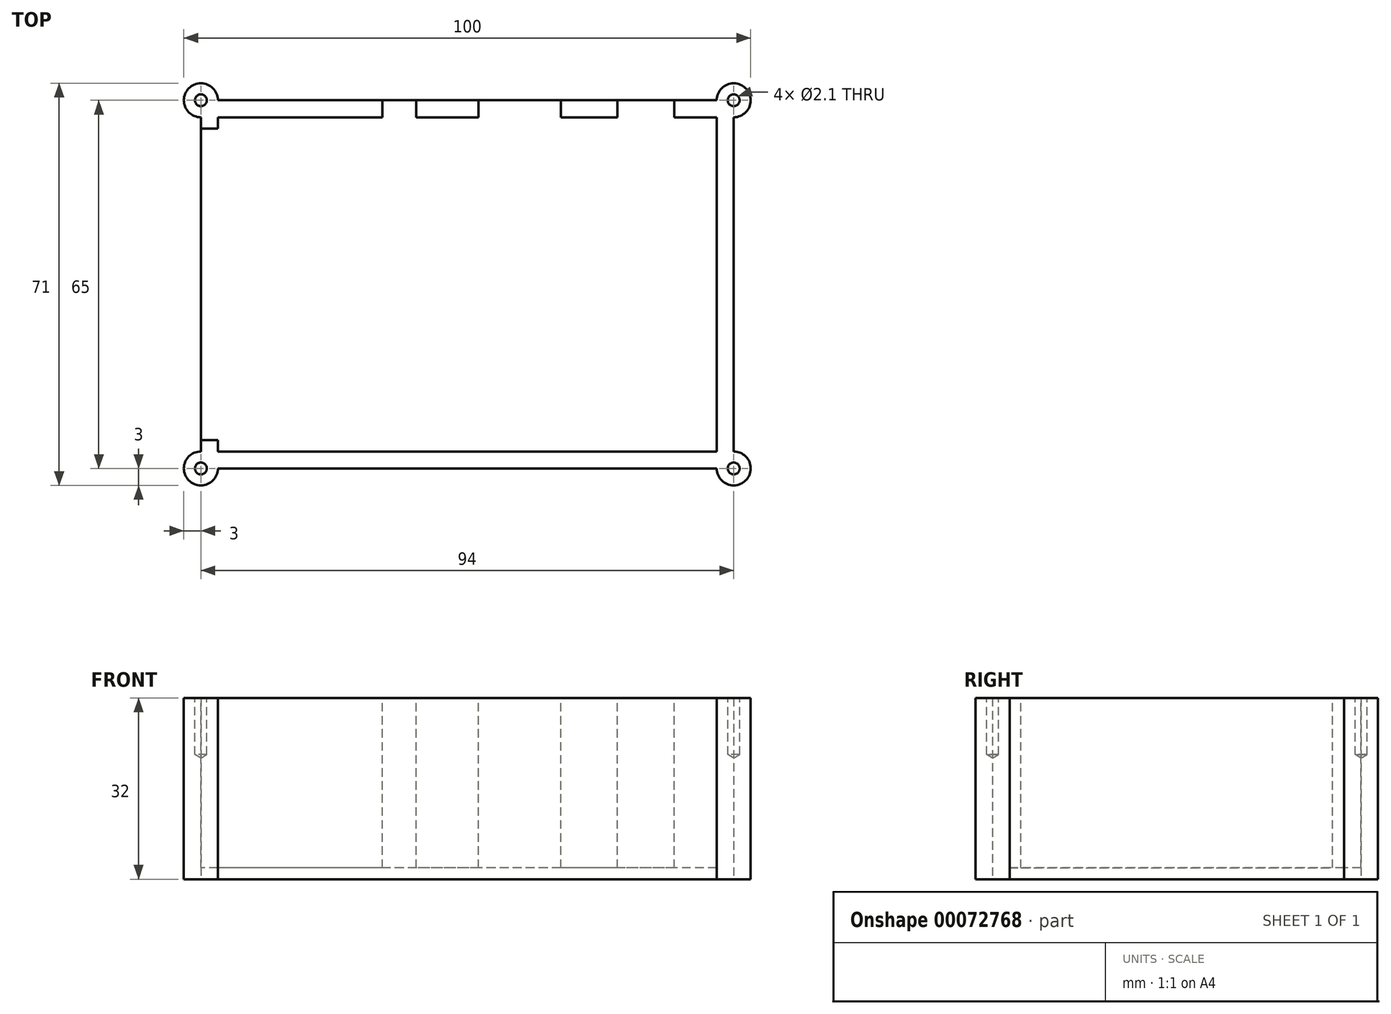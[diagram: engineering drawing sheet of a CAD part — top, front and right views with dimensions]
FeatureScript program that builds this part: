
annotation { "Feature Type Name" : "Feature", "Feature Type Description" : "" }
export const myFeature = defineFeature(function(context is Context, id is Id, definition is map)
    precondition{}
    {
        {
            var Q0;
            Q0=qCreatedBy(makeId("Top.planeOp"),FACE);
            var sketch = newSketch(context, id + "F0", { "sketchPlane" : qUnion([Q0])});
            skLineSegment(sketch, "E0.rect.bottom", {"start": v(44, -32.5) * mm, "end": v(-44, -32.5) * mm});
            skLineSegment(sketch, "E0.rect.top", {"start": v(44, 32.5) * mm, "end": v(-44, 32.5) * mm});
            skLineSegment(sketch, "E0.rect.left", {"start": v(47, -29.5) * mm, "end": v(47, 29.5) * mm});
            skLineSegment(sketch, "E0.rect.right", {"start": v(-47, -29.5) * mm, "end": v(-47, 29.5) * mm});
            skPoint(sketch, "E0.rect.middle", {"position": v(0, 0) * mm});
            skArc(sketch, "E1", {"start": v(44, -32.5) * mm, "mid": v(49.12, -34.62) * mm, "end": v(47, -29.5) * mm});
            skArc(sketch, "E2", {"start": v(47, 29.5) * mm, "mid": v(49.12, 34.62) * mm, "end": v(44, 32.5) * mm});
            skArc(sketch, "E3", {"start": v(-44, 32.5) * mm, "mid": v(-49.12, 34.62) * mm, "end": v(-47, 29.5) * mm});
            skArc(sketch, "E4", {"start": v(-47, -29.5) * mm, "mid": v(-49.12, -34.62) * mm, "end": v(-44, -32.5) * mm});
            skSolve(sketch);
        }
        {
            var Q0;
            Q0=makeQuery(id+"F0.imprint","IMPRINT",FACE,{"disambiguationData":[TD([[makeQuery(id+"F0.imprint","IMPRINT",EDGE,{"derivedFrom":sQuery(id+"F0.wireOp",EDGE,"E0.rect.bottom")}),-1.0]])]});
            extrude(context, id + "F1", {"entities" : qUnion([Q0]), "depth" : 32 * mm});
        }
        {
            var Q0;
            Q0=makeQuery(id+"F1.opExtrude","CAP_FACE",FACE,{"disambiguationData":[OSD([sQuery(id+"F0.wireOp",EDGE,"E0.rect.bottom"),sQuery(id+"F0.wireOp",EDGE,"E0.rect.top"),sQuery(id+"F0.wireOp",EDGE,"E0.rect.left"),sQuery(id+"F0.wireOp",EDGE,"E0.rect.right")])],"isStart":false});
            var sketch = newSketch(context, id + "F2", { "sketchPlane" : qUnion([Q0])});
            skPoint(sketch, "E5.rect.middle", {"position": v(0, 0) * mm});
            skLineSegment(sketch, "E6.bottom", {"start": v(44, 29.5) * mm, "end": v(36.5, 29.5) * mm});
            skLineSegment(sketch, "E6.top", {"start": v(44, -29.5) * mm, "end": v(-44, -29.5) * mm});
            skLineSegment(sketch, "E6.left", {"start": v(44, 29.5) * mm, "end": v(44, -29.5) * mm});
            skLineSegment(sketch, "E7", {"start": v(26.5, 29.5) * mm, "end": v(16.5, 29.5) * mm});
            skLineSegment(sketch, "E8", {"start": v(26.5, 29.5) * mm, "end": v(26.5, 32.5) * mm});
            skLineSegment(sketch, "E9", {"start": v(26.5, 32.5) * mm, "end": v(36.5, 32.5) * mm});
            skLineSegment(sketch, "E10", {"start": v(36.5, 32.5) * mm, "end": v(36.5, 29.5) * mm});
            skLineSegment(sketch, "E11", {"start": v(-44, 29.5) * mm, "end": v(-44, 27.5) * mm});
            skLineSegment(sketch, "E12", {"start": v(-44, 27.5) * mm, "end": v(-47, 27.5) * mm});
            skLineSegment(sketch, "E13", {"start": v(-44, -29.5) * mm, "end": v(-44, -27.5) * mm});
            skLineSegment(sketch, "E14", {"start": v(-44, -27.5) * mm, "end": v(-47, -27.5) * mm});
            skLineSegment(sketch, "E15", {"start": v(-47, 27.5) * mm, "end": v(-47, -27.5) * mm});
            skLineSegment(sketch, "E16", {"start": v(-15, 29.5) * mm, "end": v(-44, 29.5) * mm});
            skLineSegment(sketch, "E17", {"start": v(-15, 29.5) * mm, "end": v(-15, 32.5) * mm});
            skLineSegment(sketch, "E18", {"start": v(-15, 32.5) * mm, "end": v(-9, 32.5) * mm});
            skLineSegment(sketch, "E19", {"start": v(-9, 32.5) * mm, "end": v(-9, 29.5) * mm});
            skLineSegment(sketch, "E20", {"start": v(2, 29.5) * mm, "end": v(-9, 29.5) * mm});
            skLineSegment(sketch, "E21", {"start": v(2, 29.5) * mm, "end": v(2, 32.5) * mm});
            skLineSegment(sketch, "E22", {"start": v(2, 32.5) * mm, "end": v(16.5, 32.5) * mm});
            skLineSegment(sketch, "E23", {"start": v(16.5, 32.5) * mm, "end": v(16.5, 29.5) * mm});
            skSolve(sketch);
        }
        {
            var Q0;
            Q0=makeQuery(id+"F2.imprint","IMPRINT",FACE,{"disambiguationData":[TD([[makeQuery(id+"F2.imprint","IMPRINT",EDGE,{"derivedFrom":sQuery(id+"F2.wireOp",EDGE,"E6.bottom")}),1.0]])]});
            extrude(context, id + "F3", {"entities" : qUnion([Q0]), "operationType" : NewBodyOperationType.REMOVE, "oppositeDirection" : true, "depth" : 30 * mm});
        }
        {
            var Q0;
            {var subQ0=sQuery(id+"F0.wireOp",EDGE,"E0.rect.left");var subQ1=sQuery(id+"F0.wireOp",EDGE,"E4");var subQ2=sQuery(id+"F0.wireOp",EDGE,"E2");var subQ3=sQuery(id+"F0.wireOp",EDGE,"E1");var subQ4=sQuery(id+"F0.wireOp",EDGE,"E0.rect.bottom");var subQ5=sQuery(id+"F0.wireOp",EDGE,"E0.rect.top");var subQ6=sQuery(id+"F0.wireOp",EDGE,"E0.rect.right");Q0=makeQuery(id+"F3.boolean.opBoolean","SPLIT",FACE,{"disambiguationData":[TD([makeQuery(id+"F1.opExtrude","SWEPT_FACE",FACE,{"disambiguationData":[OSD([subQ4])]})])],"derivedFrom":makeQuery(id+"F1.opExtrude","CAP_FACE",FACE,{"disambiguationData":[OSD([subQ4,subQ5,subQ0,subQ6,subQ3,subQ2,sQuery(id+"F0.wireOp",EDGE,"E3"),subQ1])],"isStart":false})});}
            var sketch = newSketch(context, id + "F4", { "sketchPlane" : qUnion([Q0])});
            skPoint(sketch, "E24", {"position": v(-47, -32.5) * mm});
            skPoint(sketch, "E25", {"position": v(47, -32.5) * mm});
            skPoint(sketch, "E26", {"position": v(47, 32.5) * mm});
            skPoint(sketch, "E27", {"position": v(-47, 32.5) * mm});
            skSolve(sketch);
        }
        {
            var Q0;
            Q0=sQuery(id+"F4.wireOp",VERTEX,"E27");
            var Q1;
            Q1=sQuery(id+"F4.wireOp",VERTEX,"E26");
            var Q2;
            Q2=sQuery(id+"F4.wireOp",VERTEX,"E25");
            var Q3;
            Q3=sQuery(id+"F4.wireOp",VERTEX,"E24");
            var Q4;
            Q4=makeQuery(id+"F1.opExtrude","SWEPT_BODY",BODY,{"disambiguationData":[OSD([sQuery(id+"F0.wireOp",EDGE,"E0.rect.bottom"),sQuery(id+"F0.wireOp",EDGE,"E0.rect.top"),sQuery(id+"F0.wireOp",EDGE,"E0.rect.left"),sQuery(id+"F0.wireOp",EDGE,"E0.rect.right"),sQuery(id+"F0.wireOp",EDGE,"E1"),sQuery(id+"F0.wireOp",EDGE,"E2"),sQuery(id+"F0.wireOp",EDGE,"E3"),sQuery(id+"F0.wireOp",EDGE,"E4")])]});
            hole(context, id + "F5", {"style" : HoleStyle.SIMPLE, "holeDiameter" : 2.1 * mm, "endStyle" : HoleEndStyle.BLIND, "holeDepth" : 10 * mm, "locations" : qUnion([Q0, Q1, Q2, Q3]), "scope" : qUnion([Q4])});
        }
    });
